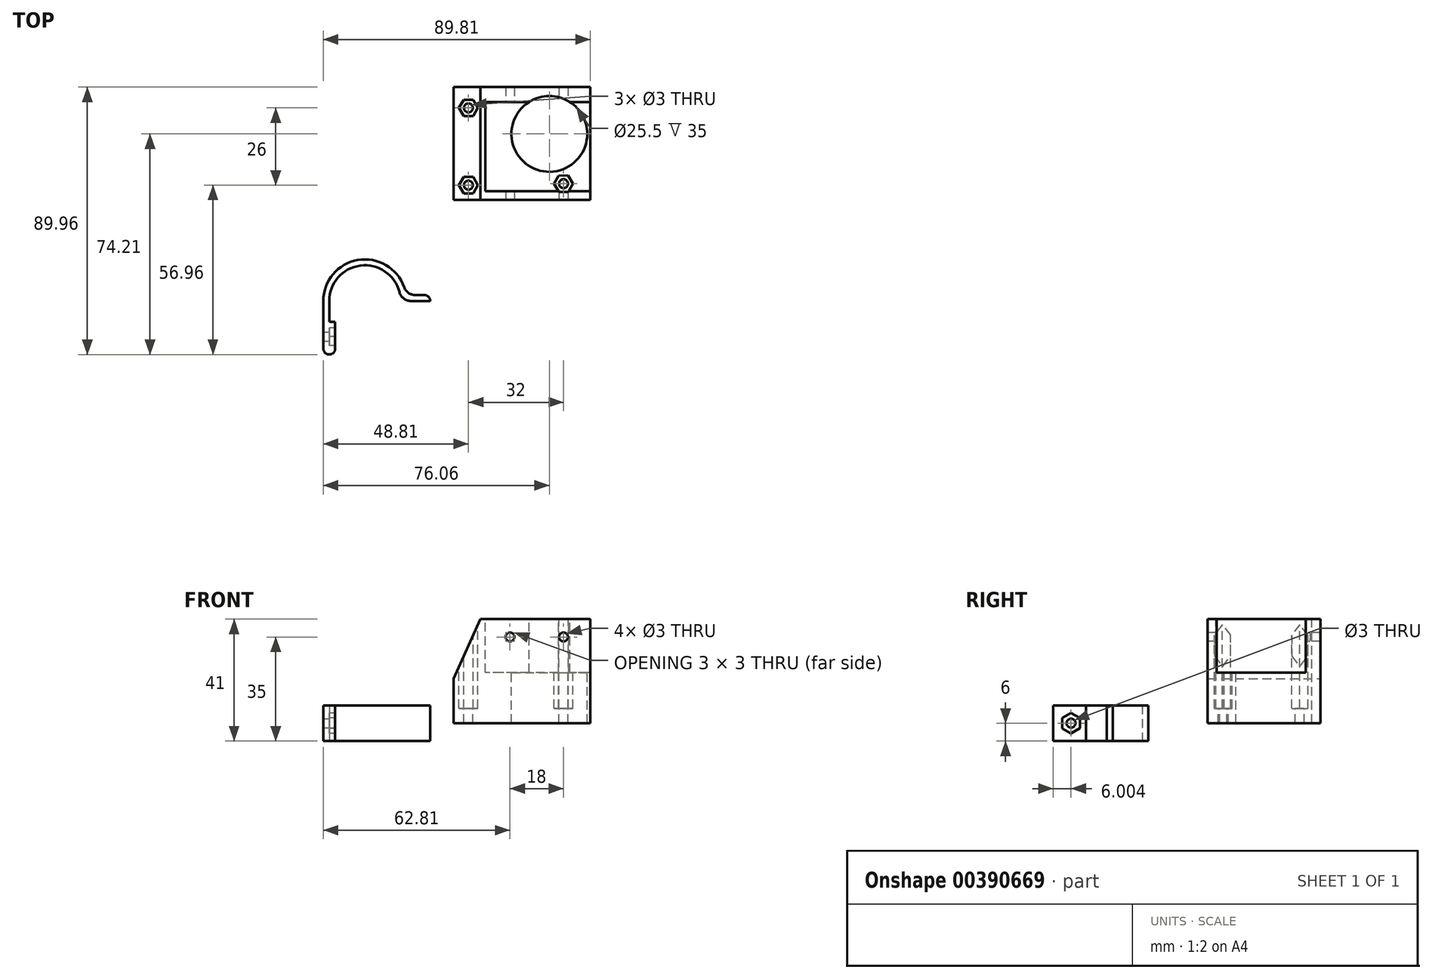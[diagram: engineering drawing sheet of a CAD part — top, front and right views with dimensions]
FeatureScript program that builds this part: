
annotation { "Feature Type Name" : "Feature", "Feature Type Description" : "" }
export const myFeature = defineFeature(function(context is Context, id is Id, definition is map)
    precondition{}
    {
        {
            var Q0;
            Q0=qCreatedBy(makeId("Top.planeOp"),FACE);
            var sketch = newSketch(context, id + "F0", { "sketchPlane" : qUnion([Q0])});
            skLineSegment(sketch, "E0.bottom", {"start": v(23, 18) * mm, "end": v(-23, 18) * mm});
            skLineSegment(sketch, "E0.top", {"start": v(23, -18) * mm, "end": v(-23, -18) * mm});
            skLineSegment(sketch, "E0.left", {"start": v(23, 18) * mm, "end": v(23, -18) * mm});
            skLineSegment(sketch, "E0.right", {"start": v(-23, 18) * mm, "end": v(-23, -18) * mm});
            skPoint(sketch, "E0.middle", {"position": v(0, 0) * mm});
            skSolve(sketch);
        }
        {
            var Q0;
            Q0=qSketchRegion(id+"F0",true);
            extrude(context, id + "F1", {"entities" : qUnion([Q0]), "depth" : 35 * mm});
        }
        {
            var Q0;
            Q0=makeQuery(id+"F1.opExtrude","CAP_FACE",FACE,{"disambiguationData":[OSD([sQuery(id+"F0.wireOp",EDGE,"E0.bottom"),sQuery(id+"F0.wireOp",EDGE,"E0.top"),sQuery(id+"F0.wireOp",EDGE,"E0.left"),sQuery(id+"F0.wireOp",EDGE,"E0.right")])],"isStart":false});
            var sketch = newSketch(context, id + "F2", { "sketchPlane" : qUnion([Q0])});
            skCircle(sketch, "E1", {"center": v(-18, -13) * mm, "radius": 1.5 * mm});
            skCircle(sketch, "E2", {"center": v(-18, 13) * mm, "radius": 1.5 * mm});
            skCircle(sketch, "E3", {"center": v(14, -12.5) * mm, "radius": 1.5 * mm});
            skCircle(sketch, "E4.cCircle", {"center": v(14, -12.5) * mm, "radius": 3.18 * mm, "construction": true});
            skLineSegment(sketch, "E4.0", {"start": v(12.44, -15.27) * mm, "end": v(10.82, -12.53) * mm});
            skLineSegment(sketch, "E4.1", {"start": v(10.82, -12.53) * mm, "end": v(12.38, -9.77) * mm});
            skLineSegment(sketch, "E4.2", {"start": v(12.38, -9.77) * mm, "end": v(15.56, -9.73) * mm});
            skLineSegment(sketch, "E4.3", {"start": v(15.56, -9.73) * mm, "end": v(17.18, -12.47) * mm});
            skLineSegment(sketch, "E4.4", {"start": v(17.18, -12.47) * mm, "end": v(15.62, -15.23) * mm});
            skLineSegment(sketch, "E4.5", {"start": v(15.62, -15.23) * mm, "end": v(12.44, -15.27) * mm});
            skCircle(sketch, "E5.cCircle", {"center": v(-18, -13) * mm, "radius": 3.18 * mm, "construction": true});
            skLineSegment(sketch, "E5.0", {"start": v(-16.4, -10.26) * mm, "end": v(-14.82, -13.02) * mm});
            skLineSegment(sketch, "E5.1", {"start": v(-14.82, -13.02) * mm, "end": v(-16.43, -15.76) * mm});
            skLineSegment(sketch, "E5.2", {"start": v(-16.43, -15.76) * mm, "end": v(-19.6, -15.74) * mm});
            skLineSegment(sketch, "E5.3", {"start": v(-19.6, -15.74) * mm, "end": v(-21.18, -12.98) * mm});
            skLineSegment(sketch, "E5.4", {"start": v(-21.18, -12.98) * mm, "end": v(-19.57, -10.24) * mm});
            skLineSegment(sketch, "E5.5", {"start": v(-19.57, -10.24) * mm, "end": v(-16.4, -10.26) * mm});
            skCircle(sketch, "E6.cCircle", {"center": v(-18, 13) * mm, "radius": 3.18 * mm, "construction": true});
            skLineSegment(sketch, "E6.0", {"start": v(-21.18, 13) * mm, "end": v(-19.59, 15.75) * mm});
            skLineSegment(sketch, "E6.1", {"start": v(-19.59, 15.75) * mm, "end": v(-16.41, 15.75) * mm});
            skLineSegment(sketch, "E6.2", {"start": v(-16.41, 15.75) * mm, "end": v(-14.82, 13) * mm});
            skLineSegment(sketch, "E6.3", {"start": v(-14.82, 13) * mm, "end": v(-16.41, 10.25) * mm});
            skLineSegment(sketch, "E6.4", {"start": v(-16.41, 10.25) * mm, "end": v(-19.59, 10.25) * mm});
            skLineSegment(sketch, "E6.5", {"start": v(-19.59, 10.25) * mm, "end": v(-21.18, 13) * mm});
            skSolve(sketch);
        }
        {
            var Q0;
            Q0=makeQuery(id+"F2.imprint","IMPRINT",FACE,{"disambiguationData":[TD([[makeQuery(id+"F2.imprint","IMPRINT",EDGE,{"derivedFrom":sQuery(id+"F2.wireOp",EDGE,"E2")}),1.0]])]});
            var Q1;
            Q1=makeQuery(id+"F2.imprint","IMPRINT",FACE,{"disambiguationData":[TD([[makeQuery(id+"F2.imprint","IMPRINT",EDGE,{"derivedFrom":sQuery(id+"F2.wireOp",EDGE,"E1")}),1.0]])]});
            var Q2;
            Q2=makeQuery(id+"F2.imprint","IMPRINT",FACE,{"disambiguationData":[TD([[makeQuery(id+"F2.imprint","IMPRINT",EDGE,{"derivedFrom":sQuery(id+"F2.wireOp",EDGE,"E3")}),1.0]])]});
            extrude(context, id + "F3", {"entities" : qUnion([Q0, Q1, Q2]), "operationType" : NewBodyOperationType.REMOVE, "oppositeDirection" : true, "depth" : 50 * mm});
        }
        {
            var Q0;
            Q0=qSketchRegion(id+"F2",true);
            extrude(context, id + "F4", {"entities" : qUnion([Q0]), "operationType" : NewBodyOperationType.REMOVE, "oppositeDirection" : true, "depth" : 30 * mm});
        }
        {
            var Q0;
            Q0=makeQuery(id+"F1.opExtrude","CAP_FACE",FACE,{"disambiguationData":[OSD([sQuery(id+"F0.wireOp",EDGE,"E0.bottom"),sQuery(id+"F0.wireOp",EDGE,"E0.top"),sQuery(id+"F0.wireOp",EDGE,"E0.left"),sQuery(id+"F0.wireOp",EDGE,"E0.right")])],"isStart":false});
            var sketch = newSketch(context, id + "F5", { "sketchPlane" : qUnion([Q0])});
            skLineSegment(sketch, "E7.bottom", {"start": v(23, -15) * mm, "end": v(-12.25, -15) * mm});
            skLineSegment(sketch, "E7.top", {"start": v(23, 15) * mm, "end": v(-12.25, 15) * mm});
            skLineSegment(sketch, "E7.left", {"start": v(23, -15) * mm, "end": v(23, 15) * mm});
            skLineSegment(sketch, "E7.right", {"start": v(-12.25, -15) * mm, "end": v(-12.25, 15) * mm});
            skSolve(sketch);
        }
        {
            var Q0;
            Q0=makeQuery(id+"F5.imprint","IMPRINT",FACE,{"disambiguationData":[TD([[makeQuery(id+"F5.imprint","IMPRINT",EDGE,{"derivedFrom":sQuery(id+"F5.wireOp",EDGE,"E7.bottom")}),-1.0]])]});
            extrude(context, id + "F6", {"entities" : qUnion([Q0]), "operationType" : NewBodyOperationType.REMOVE, "oppositeDirection" : true, "depth" : 18 * mm});
        }
        {
            var Q0;
            Q0=makeQuery(id+"F6.boolean.opBoolean","COPY",FACE,{"derivedFrom":makeQuery(id+"F6.opExtrude","CAP_FACE",FACE,{"disambiguationData":[OSD([sQuery(id+"F5.wireOp",EDGE,"E7.bottom"),sQuery(id+"F5.wireOp",EDGE,"E7.top"),sQuery(id+"F5.wireOp",EDGE,"E7.left"),sQuery(id+"F5.wireOp",EDGE,"E7.right")])],"isStart":false})});
            var sketch = newSketch(context, id + "F7", { "sketchPlane" : qUnion([Q0])});
            skCircle(sketch, "E8", {"center": v(9.25, 4.25) * mm, "radius": 12.75 * mm});
            skLineSegment(sketch, "E9", {"start": v(9.25, 4.25) * mm, "end": v(22, 4.25) * mm, "construction": true});
            skLineSegment(sketch, "E10", {"start": v(9.25, 4.25) * mm, "end": v(9.25, 17) * mm, "construction": true});
            skSolve(sketch);
        }
        {
            var Q0;
            Q0=makeQuery(id+"F7.imprint","IMPRINT",FACE,{"disambiguationData":[TD([[makeQuery(id+"F7.imprint","IMPRINT",EDGE,{"derivedFrom":sQuery(id+"F7.wireOp",EDGE,"E8")}),1.0]])]});
            extrude(context, id + "F8", {"entities" : qUnion([Q0]), "operationType" : NewBodyOperationType.REMOVE, "oppositeDirection" : true, "depth" : 50 * mm, "symmetric" : true});
        }
        {
            var Q0;
            Q0=makeQuery(id+"F6.boolean.opBoolean","COPY",FACE,{"derivedFrom":makeQuery(id+"F6.opExtrude","SWEPT_FACE",FACE,{"disambiguationData":[OSD([sQuery(id+"F5.wireOp",EDGE,"E7.top")])]})});
            var sketch = newSketch(context, id + "F9", { "sketchPlane" : qUnion([Q0])});
            skCircle(sketch, "E11", {"center": v(14, 29) * mm, "radius": 1.5 * mm});
            skCircle(sketch, "E12", {"center": v(-4, 29) * mm, "radius": 1.5 * mm});
            skSolve(sketch);
        }
        {
            var Q0;
            Q0=qSketchRegion(id+"F9",true);
            extrude(context, id + "F10", {"entities" : qUnion([Q0]), "operationType" : NewBodyOperationType.REMOVE, "oppositeDirection" : true, "depth" : 100 * mm, "symmetric" : true});
        }
        {
            var Q0;
            Q0=makeQuery(id+"F1.opExtrude","CAP_EDGE",EDGE,{"disambiguationData":[OSD([sQuery(id+"F0.wireOp",EDGE,"E0.right")])],"isStart":false});
            chamfer(context, id + "F11", {"entities" : qUnion([Q0]), "chamferType" : ChamferType.TWO_OFFSETS, "width1" : 9 * mm, "oppositeDirection" : false, "width2" : 20 * mm, "tangentPropagation" : true});
        }
        {
            var Q0;
            Q0=qCreatedBy(makeId("Top.planeOp"),FACE);
            var sketch = newSketch(context, id + "F12", { "sketchPlane" : qUnion([Q0])});
            skCircle(sketch, "E13", {"center": v(-52.8, -51.96) * mm, "radius": 12 * mm});
            skCircle(sketch, "E14.0", {"center": v(-52.8, -51.96) * mm, "radius": 14 * mm});
            skLineSegment(sketch, "E15", {"start": v(-66.8, -51.96) * mm, "end": v(-38.8, -51.96) * mm, "construction": true});
            skLineSegment(sketch, "E16.bottom", {"start": v(-66.8, -51.96) * mm, "end": v(-64.8, -51.96) * mm});
            skLineSegment(sketch, "E16.top", {"start": v(-66.8, -69.96) * mm, "end": v(-64.8, -69.96) * mm});
            skLineSegment(sketch, "E16.left", {"start": v(-66.8, -51.96) * mm, "end": v(-66.8, -69.96) * mm});
            skLineSegment(sketch, "E16.right", {"start": v(-64.8, -51.96) * mm, "end": v(-64.8, -69.96) * mm});
            skLineSegment(sketch, "E17.bottom", {"start": v(-40.8, -51.96) * mm, "end": v(-30.8, -51.96) * mm});
            skLineSegment(sketch, "E17.top", {"start": v(-40.8, -49.96) * mm, "end": v(-30.8, -49.96) * mm});
            skLineSegment(sketch, "E17.left", {"start": v(-40.8, -51.96) * mm, "end": v(-40.8, -49.96) * mm});
            skLineSegment(sketch, "E17.right", {"start": v(-30.8, -51.96) * mm, "end": v(-30.8, -49.96) * mm});
            skSolve(sketch);
        }
        {
            var Q0;
            {var subQ0=sQuery(id+"F12.wireOp",EDGE,"E16.bottom");Q0=makeQuery(id+"F12.imprint","IMPRINT",FACE,{"disambiguationData":[TD([[makeQuery(id+"F12.imprint","IMPRINT",EDGE,{"derivedFrom":subQ0}),1.0]])]});}
            var Q1;
            {var subQ5=sQuery(id+"F12.wireOp",EDGE,"E17.right");Q1=makeQuery(id+"F12.imprint","IMPRINT",FACE,{"disambiguationData":[TD([[makeQuery(id+"F12.imprint","IMPRINT",EDGE,{"derivedFrom":subQ5}),1.0]])]});}
            var Q2;
            {var subQ5=sQuery(id+"F12.wireOp",EDGE,"E17.left");Q2=makeQuery(id+"F12.imprint","IMPRINT",FACE,{"disambiguationData":[TD([[makeQuery(id+"F12.imprint","IMPRINT",EDGE,{"derivedFrom":subQ5}),-1.0]])]});}
            var Q3;
            {var subQ0=sQuery(id+"F12.wireOp",EDGE,"E16.bottom");Q3=makeQuery(id+"F12.imprint","IMPRINT",FACE,{"disambiguationData":[TD([[makeQuery(id+"F12.imprint","IMPRINT",EDGE,{"derivedFrom":subQ0}),-1.0]])]});}
            var Q4;
            {var subQ4=sQuery(id+"F12.wireOp",EDGE,"E16.top");Q4=makeQuery(id+"F12.imprint","IMPRINT",FACE,{"disambiguationData":[TD([[makeQuery(id+"F12.imprint","IMPRINT",EDGE,{"derivedFrom":subQ4}),1.0]])]});}
            extrude(context, id + "F13", {"entities" : qUnion([Q0, Q1, Q2, Q3, Q4]), "depth" : 12 * mm, "symmetric" : true});
        }
        {
            var Q0;
            Q0=makeQuery(id+"F13.opExtrude","SWEPT_FACE",FACE,{"disambiguationData":[OSD([sQuery(id+"F12.wireOp",EDGE,"E16.right")])]});
            var sketch = newSketch(context, id + "F14", { "sketchPlane" : qUnion([Q0])});
            skCircle(sketch, "E18", {"center": v(-63.96, 0) * mm, "radius": 1.5 * mm});
            skCircle(sketch, "E19.cCircle", {"center": v(-63.96, 0) * mm, "radius": 3 * mm, "construction": true});
            skLineSegment(sketch, "E19.0", {"start": v(-60.95, -1.72) * mm, "end": v(-63.94, -3.46) * mm});
            skLineSegment(sketch, "E19.1", {"start": v(-63.94, -3.46) * mm, "end": v(-66.95, -1.74) * mm});
            skLineSegment(sketch, "E19.2", {"start": v(-66.95, -1.74) * mm, "end": v(-66.96, 1.72) * mm});
            skLineSegment(sketch, "E19.3", {"start": v(-66.96, 1.72) * mm, "end": v(-63.97, 3.46) * mm});
            skLineSegment(sketch, "E19.4", {"start": v(-63.97, 3.46) * mm, "end": v(-60.96, 1.74) * mm});
            skLineSegment(sketch, "E19.5", {"start": v(-60.96, 1.74) * mm, "end": v(-60.95, -1.72) * mm});
            skPoint(sketch, "E19.0.midPoint", {"position": v(-62.45, -2.6) * mm});
            skLineSegment(sketch, "E20.bottom", {"start": v(-69.96, 6) * mm, "end": v(-58.96, 6) * mm});
            skLineSegment(sketch, "E20.top", {"start": v(-69.96, -6) * mm, "end": v(-58.96, -6) * mm});
            skLineSegment(sketch, "E20.left", {"start": v(-69.96, 6) * mm, "end": v(-69.96, -6) * mm});
            skLineSegment(sketch, "E20.right", {"start": v(-58.96, 6) * mm, "end": v(-58.96, -6) * mm});
            skSolve(sketch);
        }
        {
            var Q0;
            Q0=makeQuery(id+"F14.imprint","IMPRINT",FACE,{"disambiguationData":[TD([[makeQuery(id+"F14.imprint","IMPRINT",EDGE,{"derivedFrom":sQuery(id+"F14.wireOp",EDGE,"E19.0")}),1.0]])]});
            extrude(context, id + "F15", {"entities" : qUnion([Q0]), "operationType" : NewBodyOperationType.ADD, "depth" : 2 * mm});
        }
        {
            var Q0;
            Q0=makeQuery(id+"F14.imprint","IMPRINT",FACE,{"disambiguationData":[TD([[makeQuery(id+"F14.imprint","IMPRINT",EDGE,{"derivedFrom":sQuery(id+"F14.wireOp",EDGE,"E18")}),1.0]])]});
            extrude(context, id + "F16", {"entities" : qUnion([Q0]), "operationType" : NewBodyOperationType.REMOVE, "oppositeDirection" : true, "depth" : 25 * mm});
        }
        {
            var Q0;
            Q0=makeQuery(id+"F13.opExtrude","SWEPT_EDGE",EDGE,{"disambiguationData":[OSD([sQuery(id+"F12.wireOp",EDGE,"24572770-fc28-49ad-a867-e9377c0cc3fc.0"),sQuery(id+"F12.wireOp",EDGE,"QOivRtii-jhSI-htB5-c9gD-8GXYlo5f67iU.top")])]});
            var Q1;
            Q1=makeQuery(id+"F13.opExtrude","SWEPT_EDGE",EDGE,{"disambiguationData":[OSD([sQuery(id+"F12.wireOp",EDGE,"E14.0"),sQuery(id+"F12.wireOp",EDGE,"E17.top")])]});
            var Q2;
            Q2=makeQuery(id+"F15.opExtrude","CAP_EDGE",EDGE,{"disambiguationData":[OSD([sQuery(id+"F14.wireOp",EDGE,"E20.right")])],"isStart":true});
            var Q3;
            Q3=makeQuery(id+"F13.opExtrude","SWEPT_EDGE",EDGE,{"disambiguationData":[OSD([sQuery(id+"F12.wireOp",EDGE,"E13"),sQuery(id+"F12.wireOp",EDGE,"E17.bottom"),sQuery(id+"F12.wireOp",EDGE,"E17.left")])]});
            fillet(context, id + "F17", {"entities" : qUnion([Q0, Q1, Q2, Q3]), "radius" : 4 * mm, "tangentPropagation" : true, "allowEdgeOverflow" : false});
        }
        {
            var Q0;
            Q0=makeQuery(id+"F13.opExtrude","SWEPT_EDGE",EDGE,{"disambiguationData":[OSD([sQuery(id+"F12.wireOp",EDGE,"E16.top"),sQuery(id+"F12.wireOp",EDGE,"E16.left")])]});
            var Q1;
            Q1=makeQuery(id+"F15.opExtrude","CAP_EDGE",EDGE,{"disambiguationData":[OSD([sQuery(id+"F14.wireOp",EDGE,"E20.left")])],"isStart":false});
            var Q2;
            Q2=makeQuery(id+"F13.opExtrude","SWEPT_EDGE",EDGE,{"disambiguationData":[OSD([sQuery(id+"F12.wireOp",EDGE,"E17.top"),sQuery(id+"F12.wireOp",EDGE,"E17.right")])]});
            fillet(context, id + "F18", {"entities" : qUnion([Q0, Q1, Q2]), "radius" : 2 * mm, "tangentPropagation" : true, "allowEdgeOverflow" : false});
        }
        {
            var Q0;
            Q0=makeQuery(id+"F1.opExtrude","SWEPT_FACE",FACE,{"disambiguationData":[OSD([sQuery(id+"F0.wireOp",EDGE,"E0.bottom")])]});
            extrude(context, id + "F19", {"entities" : qUnion([Q0]), "operationType" : NewBodyOperationType.ADD, "depth" : 2 * mm, "offsetDistance" : 25 * mm});
        }
    });
